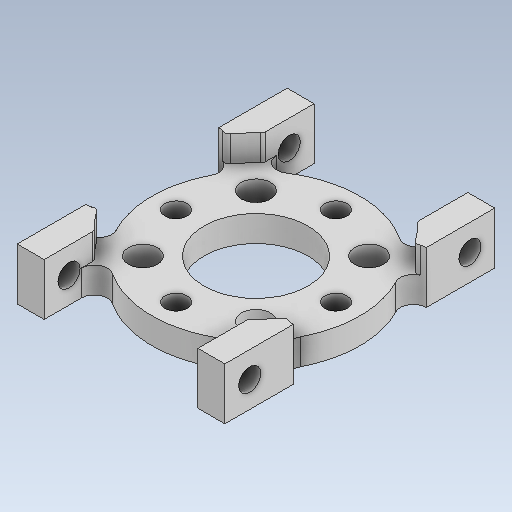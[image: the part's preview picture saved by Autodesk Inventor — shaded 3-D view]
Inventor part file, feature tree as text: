
AUTODESK INVENTOR PART (.ipt)
format: ipt  version: 2020.1 (Build 241239000, 239)  size: 190,464 bytes
history: native  units: in
note: dims shown in document units (in); Inventor stores cm internally (conversion verified against a paired STEP export)
features: mirror x1
ambient origin geometry x8: Origin, YZ Plane, XZ Plane, XY Plane, X Axis, Y Axis, Z Axis, Center Point
bodies: Solid1 (feature_tree)
feature tree (1):
  mirror  "Mirror6"
